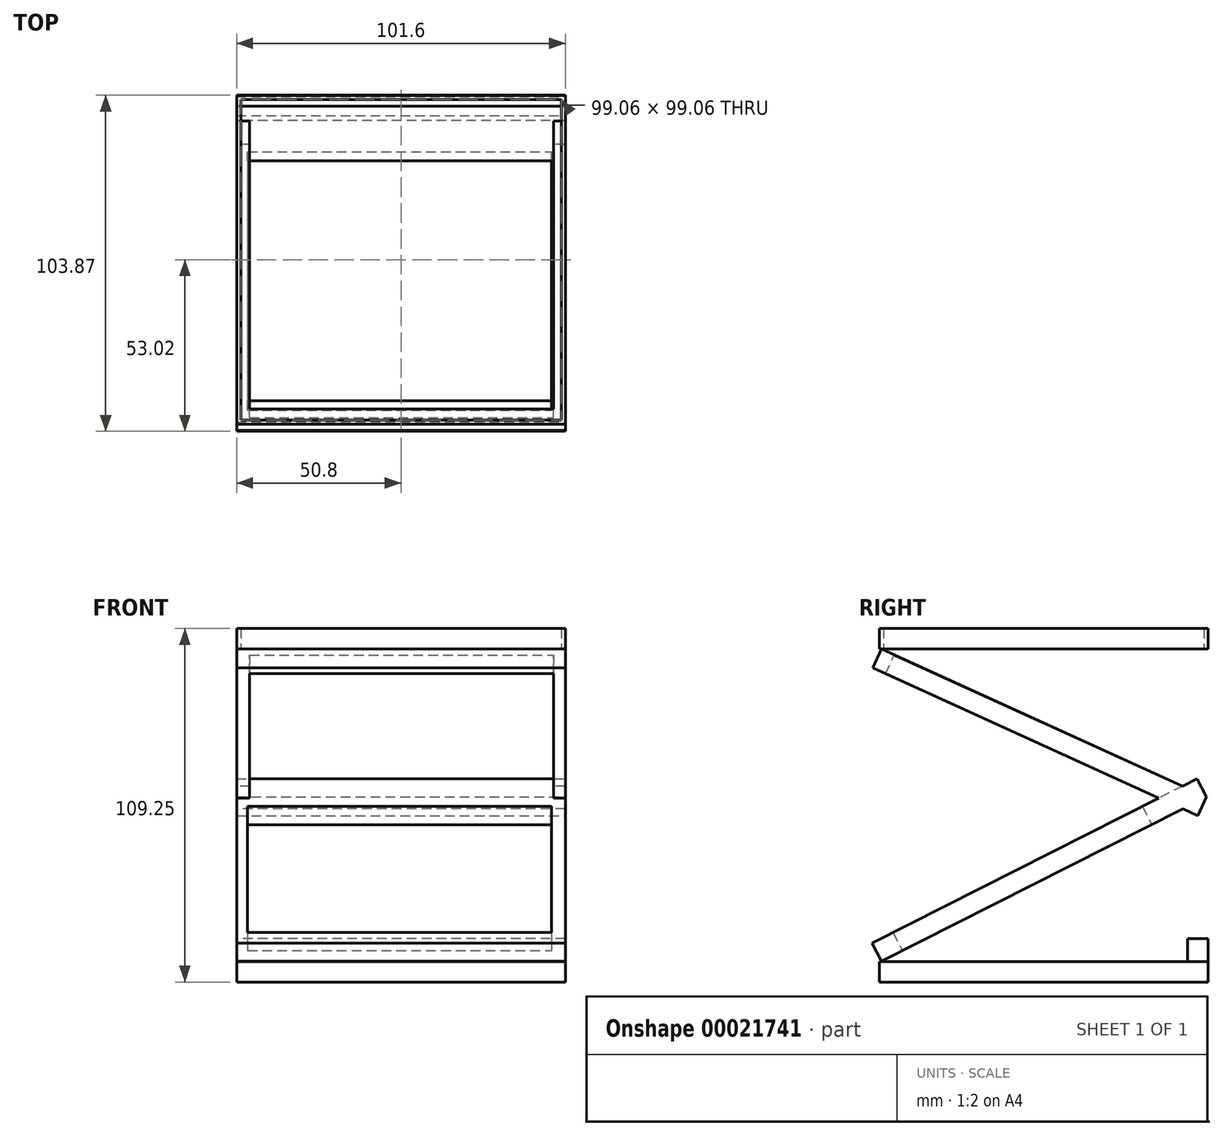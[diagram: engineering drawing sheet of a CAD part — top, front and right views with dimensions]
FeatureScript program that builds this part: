
annotation { "Feature Type Name" : "Feature", "Feature Type Description" : "" }
export const myFeature = defineFeature(function(context is Context, id is Id, definition is map)
    precondition{}
    {
        {
            var Q0;
            Q0=qCreatedBy(makeId("Top.planeOp"),FACE);
            var sketch = newSketch(context, id + "F0", { "sketchPlane" : qUnion([Q0])});
            skLineSegment(sketch, "E0.rect.bottom", {"start": v(50.8, -50.8) * mm, "end": v(-50.8, -50.8) * mm});
            skLineSegment(sketch, "E0.rect.top", {"start": v(50.8, 50.8) * mm, "end": v(-50.8, 50.8) * mm});
            skLineSegment(sketch, "E0.rect.left", {"start": v(50.8, -50.8) * mm, "end": v(50.8, 50.8) * mm});
            skLineSegment(sketch, "E0.rect.right", {"start": v(-50.8, -50.8) * mm, "end": v(-50.8, 50.8) * mm});
            skPoint(sketch, "E0.rect.middle", {"position": v(0, 0) * mm});
            skLineSegment(sketch, "E1.rect.bottom", {"start": v(49.53, -49.53) * mm, "end": v(-49.53, -49.53) * mm});
            skLineSegment(sketch, "E1.rect.top", {"start": v(49.53, 49.53) * mm, "end": v(-49.53, 49.53) * mm});
            skLineSegment(sketch, "E1.rect.left", {"start": v(49.53, -49.53) * mm, "end": v(49.53, 49.53) * mm});
            skLineSegment(sketch, "E1.rect.right", {"start": v(-49.53, -49.53) * mm, "end": v(-49.53, 49.53) * mm});
            skSolve(sketch);
        }
        {
            var Q0;
            Q0=makeQuery(id+"F0.imprint","IMPRINT",FACE,{"disambiguationData":[TD([[makeQuery(id+"F0.imprint","IMPRINT",EDGE,{"derivedFrom":sQuery(id+"F0.wireOp",EDGE,"E0.rect.bottom")}),-1.0]])]});
            extrude(context, id + "F1", {"entities" : qUnion([Q0]), "depth" : 6.35 * mm});
        }
        {
            var Q0;
            Q0=qCreatedBy(makeId("Right.planeOp"),FACE);
            var sketch = newSketch(context, id + "F2", { "sketchPlane" : qUnion([Q0])});
            skPoint(sketch, "E2.end.orphan", {"position": v(-219.39, 0) * mm});
            skPoint(sketch, "E3.start.orphan", {"position": v(219.39, 0) * mm});
            skPoint(sketch, "E4.start.orphan", {"position": v(131.6, 0) * mm});
            skPoint(sketch, "E5.start.orphan", {"position": v(-68.54, 0) * mm});
            skLineSegment(sketch, "E6", {"start": v(-50.16, 0) * mm, "end": v(50.32, -45.71) * mm});
            skPoint(sketch, "E7.start.orphan", {"position": v(50.2, 0) * mm});
            skLineSegment(sketch, "E8", {"start": v(50.32, -45.71) * mm, "end": v(-50.16, -96.51) * mm});
            skLineSegment(sketch, "E9", {"start": v(-50.16, -96.51) * mm, "end": v(50.32, -96.51) * mm});
            skPoint(sketch, "E10", {"position": v(-14.95, 35.5) * mm});
            skPoint(sketch, "E11", {"position": v(87.04, 35.5) * mm});
            skPoint(sketch, "E12.start.orphan", {"position": v(-50.16, -45.71) * mm});
            skSolve(sketch);
        }
        {
            var Q0;
            Q0=qCreatedBy(makeId("Right.planeOp"),FACE);
            var sketch = newSketch(context, id + "F3", { "sketchPlane" : qUnion([Q0])});
            skLineSegment(sketch, "E13", {"start": v(-50.75, -96.55) * mm, "end": v(50.85, -96.55) * mm});
            skSolve(sketch);
        }
        {
            var Q0;
            Q0=sQuery(id+"F2.wireOp",EDGE,"E6");
            extrude(context, id + "F4", {"bodyType" : ToolBodyType.SURFACE, "surfaceEntities" : qUnion([Q0]), "depth" : 50.8 * mm, "hasSecondDirection" : true, "secondDirectionOppositeDirection" : true, "secondDirectionDepth" : 50.8 * mm});
        }
        {
            var Q0;
            Q0=sQuery(id+"F2.wireOp",EDGE,"E8");
            extrude(context, id + "F5", {"bodyType" : ToolBodyType.SURFACE, "surfaceEntities" : qUnion([Q0]), "depth" : 50.8 * mm, "hasSecondDirection" : true, "secondDirectionOppositeDirection" : true, "secondDirectionDepth" : 50.8 * mm});
        }
        {
            var Q0;
            Q0=sQuery(id+"F3.wireOp",EDGE,"E13");
            extrude(context, id + "F6", {"bodyType" : ToolBodyType.SURFACE, "surfaceEntities" : qUnion([Q0]), "depth" : 50.8 * mm, "hasSecondDirection" : true, "secondDirectionOppositeDirection" : true, "secondDirectionDepth" : 50.8 * mm});
        }
        {
            var Q0;
            Q0=makeQuery(id+"F6.opExtrude","SWEPT_FACE",FACE,{"disambiguationData":[OSD([sQuery(id+"F3.wireOp",EDGE,"E13")])]});
            extrude(context, id + "F7", {"entities" : qUnion([Q0]), "depth" : 6.35 * mm});
        }
        {
            var Q0;
            Q0=makeQuery(id+"F4.opExtrude","SWEPT_FACE",FACE,{"disambiguationData":[OSD([sQuery(id+"F2.wireOp",EDGE,"E6")])]});
            var sketch = newSketch(context, id + "F8", { "sketchPlane" : qUnion([Q0])});
            skSolve(sketch);
        }
        {
            var Q0;
            Q0=sQuery(id+"F2.wireOp",EDGE,"E8");
            extrude(context, id + "F9", {"bodyType" : ToolBodyType.SURFACE, "surfaceEntities" : qUnion([Q0]), "depth" : 2.54 * mm});
        }
        {
            var Q0;
            Q0=makeQuery(id+"F8.imprint","IMPRINT",FACE,{"disambiguationData":[TD([[makeQuery(id+"F8.imprint","IMPRINT",EDGE,{"derivedFrom":makeQuery(id+"F4.opExtrude","SWEPT_EDGE",EDGE,{"disambiguationData":[OSD([sQuery(id+"F2.wireOp",VERTEX,"E6.start")])]})}),-1.0]])]});
            var sketch = newSketch(context, id + "F10", { "sketchPlane" : qUnion([Q0])});
            skLineSegment(sketch, "E14.bottom", {"start": v(-46.76, 41.3) * mm, "end": v(47.22, 41.3) * mm});
            skLineSegment(sketch, "E14.top", {"start": v(-46.76, -57.76) * mm, "end": v(47.22, -57.76) * mm});
            skLineSegment(sketch, "E14.left", {"start": v(-46.76, 41.3) * mm, "end": v(-46.76, -57.76) * mm});
            skLineSegment(sketch, "E14.right", {"start": v(47.22, 41.3) * mm, "end": v(47.22, -57.76) * mm});
            skSolve(sketch);
        }
        {
            var Q0;
            Q0=makeQuery(id+"F10.imprint","IMPRINT",FACE,{"disambiguationData":[TD([[makeQuery(id+"F10.imprint","IMPRINT",EDGE,{"derivedFrom":sQuery(id+"F10.wireOp",EDGE,"E14.bottom")}),1.0]])]});
            var Q1;
            Q1 = qSketchRegion(id + "F12", true);
            extrude(context, id + "F11", {"entities" : qUnion([Q0, Q1]), "depth" : 6.35 * mm});
        }
        {
            var Q0;
            Q0=makeQuery(id+"F5.opExtrude","SWEPT_FACE",FACE,{"disambiguationData":[OSD([sQuery(id+"F2.wireOp",EDGE,"E8")])]});
            var sketch = newSketch(context, id + "F12", { "sketchPlane" : qUnion([Q0])});
            skLineSegment(sketch, "E15.bottom", {"start": v(-47.42, 5.33) * mm, "end": v(46.56, 5.33) * mm});
            skLineSegment(sketch, "E15.top", {"start": v(-47.42, -81.03) * mm, "end": v(46.56, -81.03) * mm});
            skLineSegment(sketch, "E15.left", {"start": v(-47.42, 5.33) * mm, "end": v(-47.42, -81.03) * mm});
            skLineSegment(sketch, "E15.right", {"start": v(46.56, 5.33) * mm, "end": v(46.56, -81.03) * mm});
            skSolve(sketch);
        }
        {
            var Q0;
            Q0=makeQuery(id+"F12.imprint","IMPRINT",FACE,{"disambiguationData":[TD([[makeQuery(id+"F12.imprint","IMPRINT",EDGE,{"derivedFrom":sQuery(id+"F12.wireOp",EDGE,"E15.bottom")}),1.0]])]});
            extrude(context, id + "F13", {"entities" : qUnion([Q0]), "operationType" : NewBodyOperationType.ADD, "depth" : 6.35 * mm});
        }
        {
            var Q0;
            Q0=makeQuery(id+"F4.opExtrude","SWEPT_BODY",BODY,{"disambiguationData":[OSD([sQuery(id+"F2.wireOp",EDGE,"E6")])]});
            var Q1;
            Q1=makeQuery(id+"F5.opExtrude","SWEPT_BODY",BODY,{"disambiguationData":[OSD([sQuery(id+"F2.wireOp",EDGE,"E8")])]});
            deleteBodies(context, id + "F14", {"entities" : qUnion([Q0, Q1])});
        }
        {
            var Q0;
            Q0=makeQuery(id+"F7.opExtrude","SWEPT_FACE",FACE,{"disambiguationData":[OSD([sQuery(id+"F3.wireOp",VERTEX,"E13.end")])]});
            var sketch = newSketch(context, id + "F15", { "sketchPlane" : qUnion([Q0])});
            skLineSegment(sketch, "E16.bottom", {"start": v(-50.8, -96.55) * mm, "end": v(50.8, -96.55) * mm});
            skLineSegment(sketch, "E16.top", {"start": v(-50.8, -89.52) * mm, "end": v(50.8, -89.52) * mm});
            skLineSegment(sketch, "E16.left", {"start": v(-50.8, -96.55) * mm, "end": v(-50.8, -89.52) * mm});
            skLineSegment(sketch, "E16.right", {"start": v(50.8, -96.55) * mm, "end": v(50.8, -89.52) * mm});
            skSolve(sketch);
        }
        {
            var Q0;
            Q0=makeQuery(id+"F15.imprint","IMPRINT",FACE,{"disambiguationData":[TD([[makeQuery(id+"F15.imprint","IMPRINT",EDGE,{"derivedFrom":sQuery(id+"F15.wireOp",EDGE,"E16.top")}),-1.0]])]});
            extrude(context, id + "F16", {"entities" : qUnion([Q0]), "oppositeDirection" : true, "depth" : 6.35 * mm});
        }
    });
